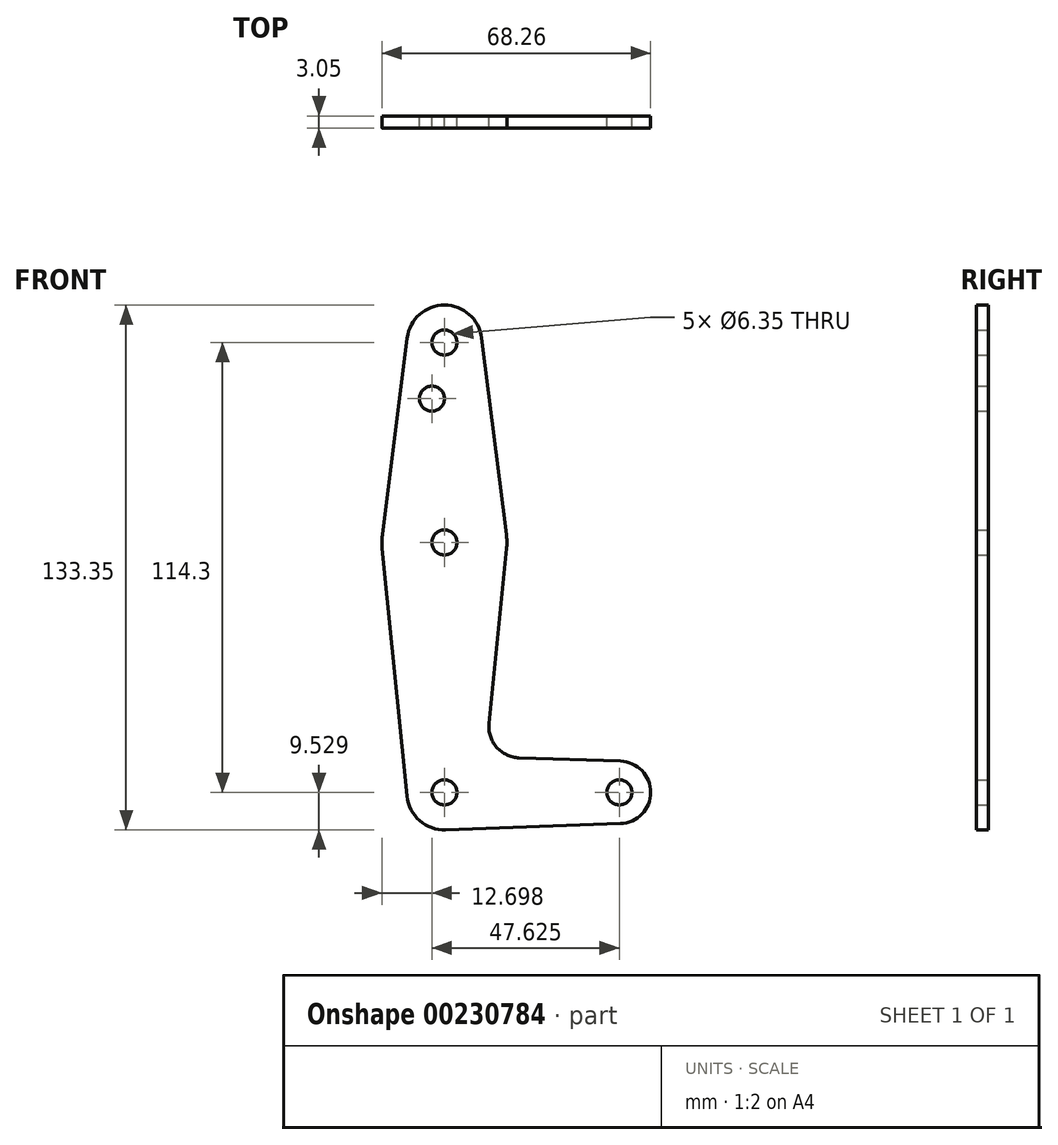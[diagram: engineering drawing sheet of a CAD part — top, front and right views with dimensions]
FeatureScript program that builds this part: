
annotation { "Feature Type Name" : "Feature", "Feature Type Description" : "" }
export const myFeature = defineFeature(function(context is Context, id is Id, definition is map)
    precondition{}
    {
        {
            var Q0;
            Q0=qCreatedBy(makeId("Front.planeOp"),FACE);
            var sketch = newSketch(context, id + "F0", { "sketchPlane" : qUnion([Q0])});
            skLineSegment(sketch, "E0", {"start": v(-49.5, 67.59) * mm, "end": v(-49.5, -37.19) * mm});
            skLineSegment(sketch, "E1", {"start": v(-49.5, -46.71) * mm, "end": v(-46.33, -46.71) * mm});
            skCircle(sketch, "E2", {"center": v(-49.5, 67.59) * mm, "radius": 9.53 * mm});
            skCircle(sketch, "E3", {"center": v(-49.5, 16.79) * mm, "radius": 15.88 * mm});
            skCircle(sketch, "E4", {"center": v(-49.5, -46.71) * mm, "radius": 9.53 * mm});
            skCircle(sketch, "E5", {"center": v(-5.06, -46.71) * mm, "radius": 7.94 * mm});
            skLineSegment(sketch, "E6", {"start": v(-33.76, 18.77) * mm, "end": v(-40.06, 68.78) * mm});
            skLineSegment(sketch, "E7", {"start": v(-38.17, -29.2) * mm, "end": v(-33.71, 15.2) * mm});
            skLineSegment(sketch, "E8", {"start": v(-49.5, -56.24) * mm, "end": v(-48.83, -56.21) * mm});
            skLineSegment(sketch, "E9", {"start": v(-65.26, 18.77) * mm, "end": v(-58.96, 68.78) * mm});
            skLineSegment(sketch, "E10.trimOffspring", {"start": v(-5.08, -54.65) * mm, "end": v(-4.46, -54.63) * mm});
            skPoint(sketch, "E11.trimOffspring.end.orphan", {"position": v(-58.98, -47.66) * mm});
            skPoint(sketch, "E12.orphan", {"position": v(-40.03, -47.66) * mm});
            skLineSegment(sketch, "E13", {"start": v(-65.3, 15.2) * mm, "end": v(-58.98, -47.66) * mm});
            skLineSegment(sketch, "E14", {"start": v(-30.52, -37.94) * mm, "end": v(-4.8, -38.78) * mm});
            skLineSegment(sketch, "E15", {"start": v(-4.77, -54.64) * mm, "end": v(-49.17, -56.23) * mm});
            skLineSegment(sketch, "E16", {"start": v(-49.17, -56.23) * mm, "end": v(-49.43, -55.58) * mm});
            skCircle(sketch, "E17", {"center": v(-52.68, 53.31) * mm, "radius": 3.18 * mm});
            skCircle(sketch, "E18", {"center": v(-49.5, 67.59) * mm, "radius": 3.18 * mm});
            skCircle(sketch, "E19", {"center": v(-49.5, 16.79) * mm, "radius": 3.18 * mm});
            skCircle(sketch, "E20", {"center": v(-49.5, -46.71) * mm, "radius": 3.18 * mm});
            skCircle(sketch, "E21", {"center": v(-5.06, -46.71) * mm, "radius": 3.18 * mm});
            skArc(sketch, "E22.filletArc", {"start": v(-38.17, -29.2) * mm, "mid": v(-36.25, -35.23) * mm, "end": v(-30.52, -37.94) * mm});
            skSolve(sketch);
        }
        {
            var Q0;
            Q0 = qSketchRegion(id + "F0", true);
            extrude(context, id + "F1", {"entities" : qUnion([Q0]), "depth" : 3.05 * mm});
        }
    });
